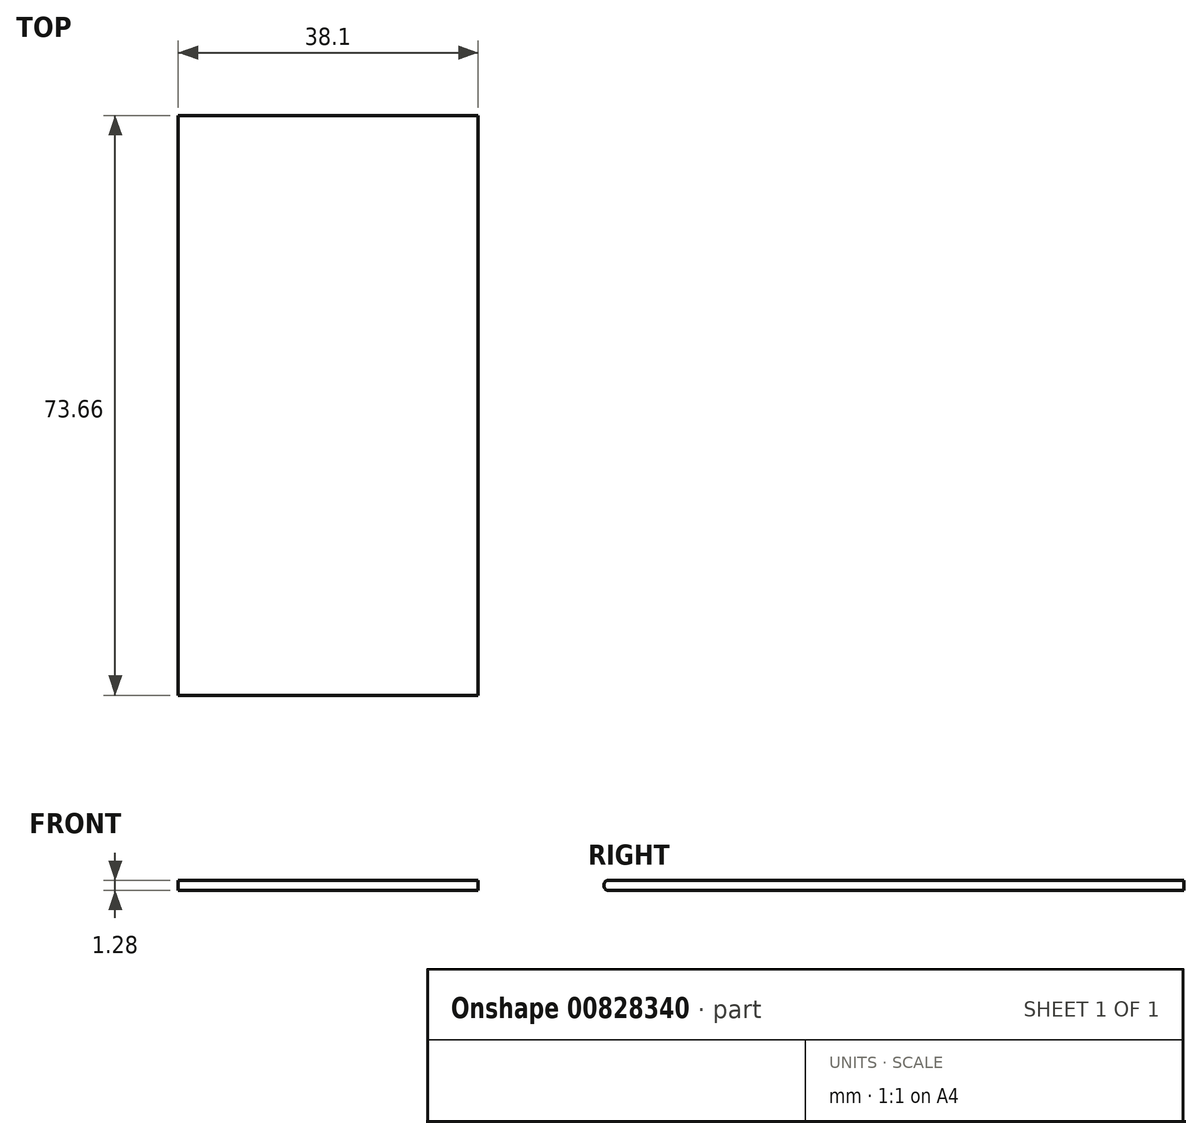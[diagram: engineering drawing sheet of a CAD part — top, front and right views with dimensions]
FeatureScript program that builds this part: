
annotation { "Feature Type Name" : "Feature", "Feature Type Description" : "" }
export const myFeature = defineFeature(function(context is Context, id is Id, definition is map)
    precondition{}
    {
        {
            var Q0;
            Q0=qCreatedBy(makeId("Front.planeOp"),FACE);
            var sketch = newSketch(context, id + "F0", { "sketchPlane" : qUnion([Q0])});
            skLineSegment(sketch, "E0.bottom", {"start": v(19.05, 0.63) * mm, "end": v(-19.05, 0.64) * mm});
            skLineSegment(sketch, "E0.top", {"start": v(19.05, -0.64) * mm, "end": v(-19.05, -0.63) * mm});
            skLineSegment(sketch, "E0.left", {"start": v(19.05, 0.64) * mm, "end": v(19.05, -0.64) * mm});
            skLineSegment(sketch, "E0.right", {"start": v(-19.05, 0.63) * mm, "end": v(-19.05, -0.63) * mm});
            skPoint(sketch, "E0.middle", {"position": v(0, 0) * mm});
            skLineSegment(sketch, "E1.left", {"start": v(19.05, 0) * mm, "end": v(19.05, 0) * mm});
            skPoint(sketch, "E1.middle", {"position": v(-19.05, 0) * mm});
            skSolve(sketch);
        }
        {
            var Q0;
            Q0 = qSketchRegion(id + "F0", true);
            extrude(context, id + "F1", {"entities" : qUnion([Q0]), "oppositeDirection" : true, "depth" : 73.66 * mm, "offsetDistance" : 25.4 * mm});
        }
        {
            var Q0;
            Q0=makeQuery(id+"F1.opExtrude","CAP_EDGE",EDGE,{"disambiguationData":[OSD([sQuery(id+"F0.wireOp",EDGE,"E0.bottom")])],"isStart":true});
            var Q1;
            Q1=makeQuery(id+"F1.opExtrude","CAP_EDGE",EDGE,{"disambiguationData":[OSD([sQuery(id+"F0.wireOp",EDGE,"E0.top")])],"isStart":true});
            fillet(context, id + "F2", {"entities" : qUnion([Q0, Q1]), "radius" : 0.5 * mm, "tangentPropagation" : true, "allowEdgeOverflow" : false});
        }
    });
